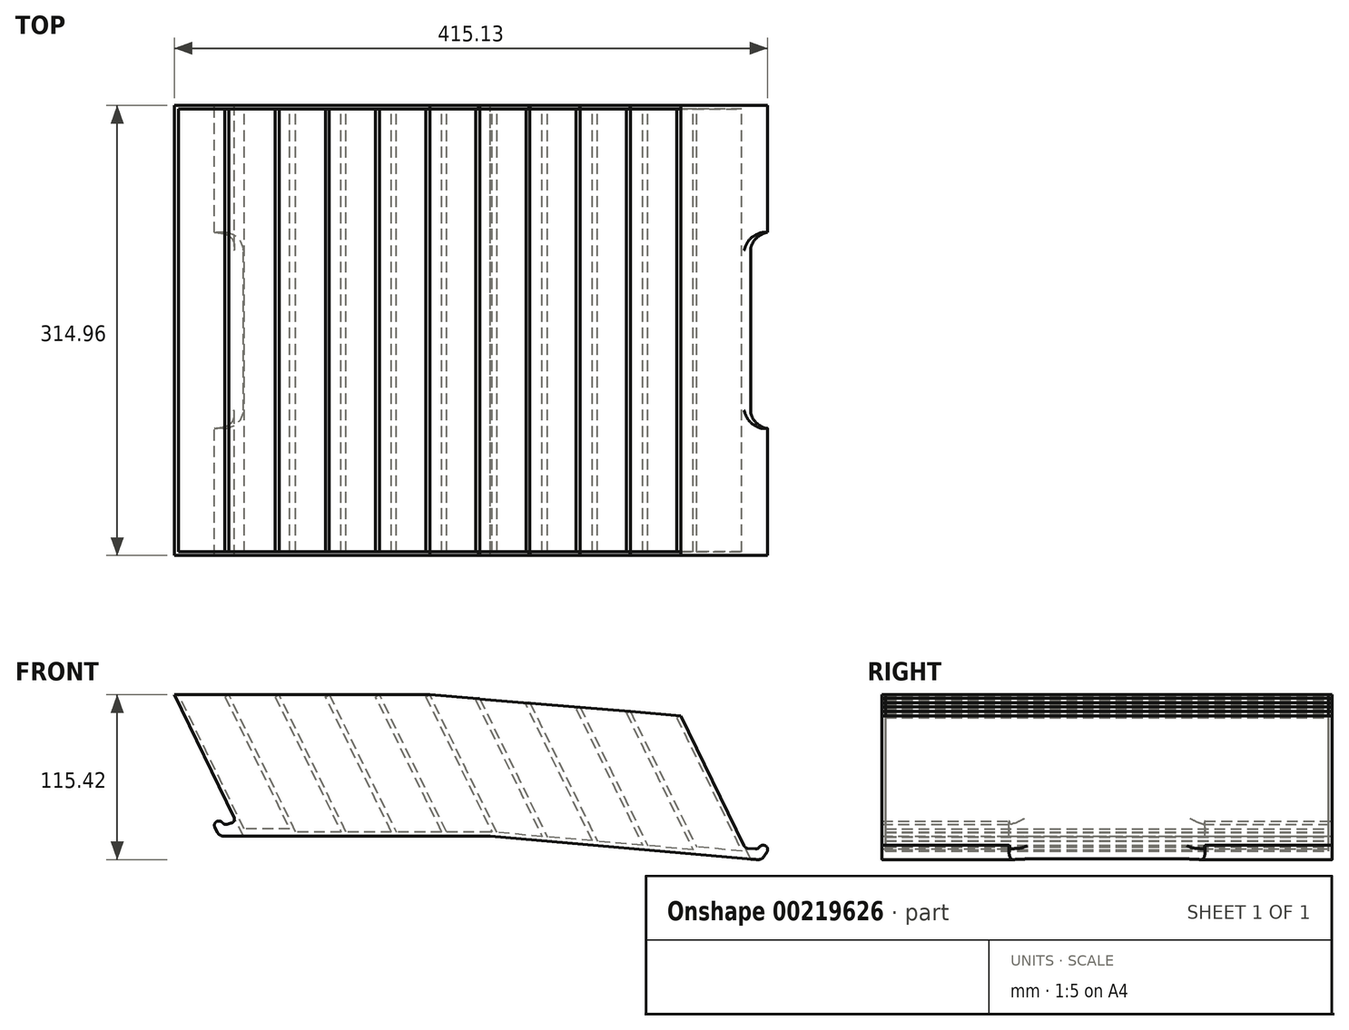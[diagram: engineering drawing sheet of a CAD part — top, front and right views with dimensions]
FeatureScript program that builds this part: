
annotation { "Feature Type Name" : "Feature", "Feature Type Description" : "" }
export const myFeature = defineFeature(function(context is Context, id is Id, definition is map)
    precondition{}
    {
        {
            var Q0;
            Q0=qCreatedBy(makeId("Front.planeOp"),FACE);
            var sketch = newSketch(context, id + "F0", { "sketchPlane" : qUnion([Q0])});
            skLineSegment(sketch, "E0", {"start": v(0, 0) * mm, "end": v(189.48, 0) * mm});
            skLineSegment(sketch, "E1", {"start": v(189.48, 0) * mm, "end": v(379.26, -16.6) * mm});
            skLineSegment(sketch, "E2", {"start": v(367.73, -8.25) * mm, "end": v(332.9, 63.16) * mm});
            skLineSegment(sketch, "E3", {"start": v(332.9, 63.16) * mm, "end": v(330.16, 61.83) * mm, "construction": true});
            skLineSegment(sketch, "E4", {"start": v(330.16, 61.83) * mm, "end": v(365.33, -10.29) * mm});
            skLineSegment(sketch, "E5", {"start": v(11.64, 10.16) * mm, "end": v(-21.71, 78.55) * mm});
            skLineSegment(sketch, "E6", {"start": v(-21.71, 78.55) * mm, "end": v(-18.66, 78.55) * mm});
            skLineSegment(sketch, "E7", {"start": v(-18.66, 78.55) * mm, "end": v(17.17, 5.08) * mm});
            skLineSegment(sketch, "E8", {"start": v(17.17, 5.08) * mm, "end": v(48.92, 5.08) * mm});
            skLineSegment(sketch, "E9", {"start": v(48.92, 5.08) * mm, "end": v(13.74, 77.21) * mm});
            skLineSegment(sketch, "E10", {"start": v(13.74, 77.21) * mm, "end": v(16.48, 78.55) * mm});
            skLineSegment(sketch, "E11", {"start": v(16.48, 78.55) * mm, "end": v(52.31, 5.08) * mm});
            skLineSegment(sketch, "E12", {"start": v(52.31, 5.08) * mm, "end": v(84.06, 5.08) * mm, "construction": true});
            skLineSegment(sketch, "E13", {"start": v(84.06, 5.08) * mm, "end": v(48.88, 77.21) * mm});
            skLineSegment(sketch, "E14", {"start": v(48.88, 77.21) * mm, "end": v(51.62, 78.55) * mm, "construction": true});
            skLineSegment(sketch, "E15", {"start": v(51.62, 78.55) * mm, "end": v(87.45, 5.08) * mm});
            skLineSegment(sketch, "E16", {"start": v(87.45, 5.08) * mm, "end": v(119.2, 5.08) * mm, "construction": true});
            skLineSegment(sketch, "E17", {"start": v(119.2, 5.08) * mm, "end": v(84.02, 77.21) * mm});
            skLineSegment(sketch, "E18", {"start": v(86.76, 78.55) * mm, "end": v(122.6, 5.08) * mm});
            skLineSegment(sketch, "E19", {"start": v(122.6, 5.08) * mm, "end": v(154.34, 5.08) * mm, "construction": true});
            skLineSegment(sketch, "E20", {"start": v(154.34, 5.08) * mm, "end": v(119.16, 77.21) * mm});
            skLineSegment(sketch, "E21", {"start": v(119.16, 77.21) * mm, "end": v(121.9, 78.55) * mm, "construction": true});
            skLineSegment(sketch, "E22", {"start": v(121.9, 78.55) * mm, "end": v(157.73, 5.08) * mm});
            skLineSegment(sketch, "E23", {"start": v(157.73, 5.08) * mm, "end": v(189.48, 5.08) * mm, "construction": true});
            skLineSegment(sketch, "E24", {"start": v(189.48, 0) * mm, "end": v(189.48, 5.08) * mm, "construction": true});
            skLineSegment(sketch, "E25", {"start": v(189.48, 5.08) * mm, "end": v(154.3, 77.21) * mm});
            skLineSegment(sketch, "E26", {"start": v(154.3, 77.21) * mm, "end": v(157.04, 78.55) * mm, "construction": true});
            skLineSegment(sketch, "E27", {"start": v(157.04, 78.55) * mm, "end": v(193.02, 4.8) * mm});
            skLineSegment(sketch, "E28", {"start": v(193.02, 4.8) * mm, "end": v(224.65, 2.02) * mm, "construction": true});
            skLineSegment(sketch, "E29", {"start": v(224.65, 2.02) * mm, "end": v(189.47, 74.14) * mm});
            skLineSegment(sketch, "E30", {"start": v(189.47, 74.14) * mm, "end": v(192.21, 75.47) * mm, "construction": true});
            skLineSegment(sketch, "E31", {"start": v(192.21, 75.47) * mm, "end": v(228.19, 1.71) * mm});
            skLineSegment(sketch, "E32", {"start": v(224.65, 2.02) * mm, "end": v(228.19, 1.71) * mm, "construction": true});
            skLineSegment(sketch, "E33", {"start": v(228.19, 1.71) * mm, "end": v(259.82, -1.05) * mm, "construction": true});
            skLineSegment(sketch, "E34", {"start": v(259.82, -1.05) * mm, "end": v(224.65, 71.06) * mm});
            skLineSegment(sketch, "E35", {"start": v(224.65, 71.06) * mm, "end": v(227.39, 72.4) * mm, "construction": true});
            skLineSegment(sketch, "E36", {"start": v(227.39, 72.4) * mm, "end": v(263.36, -1.36) * mm});
            skLineSegment(sketch, "E37", {"start": v(263.36, -1.36) * mm, "end": v(294.99, -4.13) * mm, "construction": true});
            skLineSegment(sketch, "E38", {"start": v(294.99, -4.13) * mm, "end": v(259.82, 67.98) * mm});
            skLineSegment(sketch, "E39", {"start": v(259.82, 67.98) * mm, "end": v(262.56, 69.32) * mm, "construction": true});
            skLineSegment(sketch, "E40", {"start": v(262.56, 69.32) * mm, "end": v(298.53, -4.44) * mm});
            skLineSegment(sketch, "E41", {"start": v(298.53, -4.44) * mm, "end": v(330.16, -7.2) * mm, "construction": true});
            skLineSegment(sketch, "E42", {"start": v(330.16, -7.2) * mm, "end": v(294.99, 64.9) * mm});
            skLineSegment(sketch, "E43", {"start": v(294.99, 64.9) * mm, "end": v(297.73, 66.24) * mm, "construction": true});
            skLineSegment(sketch, "E44", {"start": v(297.73, 66.24) * mm, "end": v(333.7, -7.52) * mm});
            skLineSegment(sketch, "E45", {"start": v(333.7, -7.52) * mm, "end": v(365.33, -10.29) * mm});
            skLineSegment(sketch, "E46", {"start": v(-18.66, 78.55) * mm, "end": v(157.04, 78.55) * mm, "construction": true});
            skLineSegment(sketch, "E47", {"start": v(157.04, 78.55) * mm, "end": v(332.9, 63.16) * mm, "construction": true});
            skLineSegment(sketch, "E48", {"start": v(84.02, 77.21) * mm, "end": v(86.76, 78.55) * mm, "construction": true});
            skLineSegment(sketch, "E49", {"start": v(367.73, -8.25) * mm, "end": v(376.94, -9.06) * mm});
            skLineSegment(sketch, "E50", {"start": v(379.26, -16.6) * mm, "end": v(383.77, -9.65) * mm});
            skArc(sketch, "E51", {"start": v(383.77, -9.65) * mm, "mid": v(380.63, -6.27) * mm, "end": v(376.94, -9.06) * mm});
            skLineSegment(sketch, "E52", {"start": v(376.94, -9.06) * mm, "end": v(383.77, -9.65) * mm, "construction": true});
            skLineSegment(sketch, "E53", {"start": v(0, 0) * mm, "end": v(-4.05, 7.62) * mm});
            skLineSegment(sketch, "E54", {"start": v(11.64, 10.16) * mm, "end": v(2.8, 7.62) * mm});
            skArc(sketch, "E55", {"start": v(2.8, 7.62) * mm, "mid": v(-0.62, 10.67) * mm, "end": v(-4.05, 7.62) * mm});
            skLineSegment(sketch, "E56", {"start": v(-4.05, 7.62) * mm, "end": v(2.8, 7.62) * mm, "construction": true});
            skLineSegment(sketch, "E57", {"start": v(-21.71, 78.55) * mm, "end": v(-31.72, 99.06) * mm});
            skLineSegment(sketch, "E58", {"start": v(-31.72, 99.06) * mm, "end": v(-28.67, 99.06) * mm});
            skLineSegment(sketch, "E59", {"start": v(-28.67, 99.06) * mm, "end": v(-18.66, 78.55) * mm});
            skLineSegment(sketch, "E60", {"start": v(13.74, 77.21) * mm, "end": v(3.73, 97.72) * mm});
            skLineSegment(sketch, "E61", {"start": v(3.73, 97.72) * mm, "end": v(6.47, 99.06) * mm});
            skLineSegment(sketch, "E62", {"start": v(6.47, 99.06) * mm, "end": v(16.48, 78.55) * mm});
            skLineSegment(sketch, "E63", {"start": v(48.88, 77.21) * mm, "end": v(38.87, 97.72) * mm});
            skLineSegment(sketch, "E64", {"start": v(38.87, 97.72) * mm, "end": v(41.61, 99.06) * mm});
            skLineSegment(sketch, "E65", {"start": v(41.61, 99.06) * mm, "end": v(51.62, 78.55) * mm});
            skLineSegment(sketch, "E66", {"start": v(109.16, 97.72) * mm, "end": v(111.9, 99.06) * mm});
            skLineSegment(sketch, "E67", {"start": v(259.82, 67.98) * mm, "end": v(249.49, 89.16) * mm});
            skLineSegment(sketch, "E68", {"start": v(249.49, 89.16) * mm, "end": v(252.23, 90.5) * mm});
            skLineSegment(sketch, "E69", {"start": v(252.23, 90.5) * mm, "end": v(262.56, 69.32) * mm});
            skLineSegment(sketch, "E70", {"start": v(330.16, 61.83) * mm, "end": v(319.83, 83) * mm});
            skLineSegment(sketch, "E71", {"start": v(319.83, 83) * mm, "end": v(322.57, 84.34) * mm});
            skLineSegment(sketch, "E72", {"start": v(322.57, 84.34) * mm, "end": v(332.9, 63.16) * mm});
            skLineSegment(sketch, "E73", {"start": v(154.3, 77.21) * mm, "end": v(144.3, 97.72) * mm});
            skLineSegment(sketch, "E74", {"start": v(294.99, 64.9) * mm, "end": v(284.66, 86.08) * mm});
            skLineSegment(sketch, "E75", {"start": v(189.47, 74.14) * mm, "end": v(179.15, 95.31) * mm});
            skLineSegment(sketch, "E76", {"start": v(-28.67, 99.06) * mm, "end": v(154.3, 99.06) * mm, "construction": true});
            skLineSegment(sketch, "E77", {"start": v(322.57, 84.34) * mm, "end": v(154.3, 99.06) * mm, "construction": true});
            skLineSegment(sketch, "E78", {"start": v(86.76, 78.55) * mm, "end": v(76.76, 99.06) * mm});
            skLineSegment(sketch, "E79", {"start": v(76.76, 99.06) * mm, "end": v(74.02, 97.72) * mm});
            skLineSegment(sketch, "E80", {"start": v(74.02, 97.72) * mm, "end": v(84.02, 77.21) * mm});
            skLineSegment(sketch, "E81", {"start": v(109.16, 97.72) * mm, "end": v(119.16, 77.21) * mm});
            skLineSegment(sketch, "E82", {"start": v(111.9, 99.06) * mm, "end": v(121.9, 78.55) * mm});
            skLineSegment(sketch, "E83", {"start": v(157.04, 78.55) * mm, "end": v(147.04, 99.06) * mm});
            skLineSegment(sketch, "E84", {"start": v(147.04, 99.06) * mm, "end": v(144.3, 97.72) * mm});
            skLineSegment(sketch, "E85", {"start": v(192.21, 75.47) * mm, "end": v(181.89, 96.65) * mm});
            skLineSegment(sketch, "E86", {"start": v(181.89, 96.65) * mm, "end": v(179.15, 95.31) * mm});
            skLineSegment(sketch, "E87", {"start": v(227.39, 72.4) * mm, "end": v(217.06, 93.57) * mm});
            skLineSegment(sketch, "E88", {"start": v(217.06, 93.57) * mm, "end": v(214.32, 92.23) * mm});
            skLineSegment(sketch, "E89", {"start": v(214.32, 92.23) * mm, "end": v(224.65, 71.06) * mm});
            skLineSegment(sketch, "E90", {"start": v(297.73, 66.24) * mm, "end": v(287.4, 87.42) * mm});
            skLineSegment(sketch, "E91", {"start": v(287.4, 87.42) * mm, "end": v(284.66, 86.08) * mm});
            skLineSegment(sketch, "E92", {"start": v(52.31, 5.08) * mm, "end": v(53.3, 3.05) * mm});
            skLineSegment(sketch, "E93", {"start": v(53.3, 3.05) * mm, "end": v(189.48, 3.05) * mm});
            skLineSegment(sketch, "E94", {"start": v(189.48, 3.05) * mm, "end": v(331.2, -9.35) * mm});
            skLineSegment(sketch, "E95", {"start": v(331.2, -9.35) * mm, "end": v(330.16, -7.2) * mm});
            skLineSegment(sketch, "E96", {"start": v(84.06, 5.08) * mm, "end": v(85.05, 3.05) * mm});
            skLineSegment(sketch, "E97", {"start": v(87.45, 5.08) * mm, "end": v(88.44, 3.05) * mm});
            skLineSegment(sketch, "E98", {"start": v(119.2, 5.08) * mm, "end": v(120.2, 3.05) * mm});
            skLineSegment(sketch, "E99", {"start": v(122.6, 5.08) * mm, "end": v(123.58, 3.05) * mm});
            skLineSegment(sketch, "E100", {"start": v(154.34, 5.08) * mm, "end": v(155.33, 3.05) * mm});
            skLineSegment(sketch, "E101", {"start": v(157.73, 5.08) * mm, "end": v(158.73, 3.05) * mm});
            skLineSegment(sketch, "E102", {"start": v(189.48, 5.08) * mm, "end": v(190.52, 2.96) * mm});
            skLineSegment(sketch, "E103", {"start": v(193.02, 4.8) * mm, "end": v(194.06, 2.65) * mm});
            skLineSegment(sketch, "E104", {"start": v(224.65, 2.02) * mm, "end": v(225.7, -0.12) * mm});
            skLineSegment(sketch, "E105", {"start": v(228.19, 1.71) * mm, "end": v(229.23, -0.43) * mm});
            skLineSegment(sketch, "E106", {"start": v(259.82, -1.05) * mm, "end": v(260.86, -3.2) * mm});
            skLineSegment(sketch, "E107", {"start": v(263.36, -1.36) * mm, "end": v(264.4, -3.5) * mm});
            skLineSegment(sketch, "E108", {"start": v(294.99, -4.13) * mm, "end": v(296.03, -6.27) * mm});
            skLineSegment(sketch, "E109", {"start": v(298.53, -4.44) * mm, "end": v(299.58, -6.58) * mm});
            skSolve(sketch);
        }
        {
            var Q0;
            Q0=qSketchRegion(id+"F0",true);
            extrude(context, id + "F1", {"entities" : qUnion([Q0]), "endBound" : BoundingType.SYMMETRIC, "depth" : 314.96 * mm});
        }
        {
            var Q0;
            Q0=makeQuery(id+"F1.opExtrude","SWEPT_EDGE",EDGE,{"disambiguationData":[OSD([sQuery(id+"F0.wireOp",EDGE,"E5"),sQuery(id+"F0.wireOp",EDGE,"E54")])]});
            var Q1;
            Q1=makeQuery(id+"F1.opExtrude","SWEPT_EDGE",EDGE,{"disambiguationData":[OSD([sQuery(id+"F0.wireOp",EDGE,"E54"),sQuery(id+"F0.wireOp",EDGE,"E55")])]});
            var Q2;
            Q2=makeQuery(id+"F1.opExtrude","SWEPT_EDGE",EDGE,{"disambiguationData":[OSD([sQuery(id+"F0.wireOp",EDGE,"E2"),sQuery(id+"F0.wireOp",EDGE,"E49")])]});
            var Q3;
            Q3=makeQuery(id+"F1.opExtrude","SWEPT_EDGE",EDGE,{"disambiguationData":[OSD([sQuery(id+"F0.wireOp",EDGE,"E49"),sQuery(id+"F0.wireOp",EDGE,"E51")])]});
            var Q4;
            Q4=makeQuery(id+"F1.opExtrude","SWEPT_EDGE",EDGE,{"disambiguationData":[OSD([sQuery(id+"F0.wireOp",EDGE,"E50"),sQuery(id+"F0.wireOp",EDGE,"E51")])]});
            var Q5;
            Q5=makeQuery(id+"F1.opExtrude","SWEPT_EDGE",EDGE,{"disambiguationData":[OSD([sQuery(id+"F0.wireOp",EDGE,"E53"),sQuery(id+"F0.wireOp",EDGE,"E55")])]});
            fillet(context, id + "F2", {"entities" : qUnion([Q0, Q1, Q2, Q3, Q4, Q5]), "radius" : 3.05 * mm, "tangentPropagation" : true, "allowEdgeOverflow" : false});
        }
        {
            var Q0;
            Q0=makeQuery(id+"F1.opExtrude","SWEPT_EDGE",EDGE,{"disambiguationData":[OSD([sQuery(id+"F0.wireOp",EDGE,"E0"),sQuery(id+"F0.wireOp",EDGE,"E53")])]});
            var Q1;
            Q1=makeQuery(id+"F1.opExtrude","SWEPT_EDGE",EDGE,{"disambiguationData":[OSD([sQuery(id+"F0.wireOp",EDGE,"E1"),sQuery(id+"F0.wireOp",EDGE,"E50")])]});
            fillet(context, id + "F3", {"entities" : qUnion([Q0, Q1]), "radius" : 5.08 * mm, "tangentPropagation" : true, "allowEdgeOverflow" : false});
        }
        {
            var Q0;
            Q0=makeQuery(id+"F1.opExtrude","CAP_FACE",FACE,{"disambiguationData":[OSD([sQuery(id+"F0.wireOp",EDGE,"E0"),sQuery(id+"F0.wireOp",EDGE,"E1"),sQuery(id+"F0.wireOp",EDGE,"E2"),sQuery(id+"F0.wireOp",EDGE,"E3"),sQuery(id+"F0.wireOp",EDGE,"E4"),sQuery(id+"F0.wireOp",EDGE,"E5"),sQuery(id+"F0.wireOp",EDGE,"E6"),sQuery(id+"F0.wireOp",EDGE,"E7"),sQuery(id+"F0.wireOp",EDGE,"E8"),sQuery(id+"F0.wireOp",EDGE,"E9"),sQuery(id+"F0.wireOp",EDGE,"E10"),sQuery(id+"F0.wireOp",EDGE,"E11"),sQuery(id+"F0.wireOp",EDGE,"E12"),sQuery(id+"F0.wireOp",EDGE,"E13"),sQuery(id+"F0.wireOp",EDGE,"E14"),sQuery(id+"F0.wireOp",EDGE,"E15"),sQuery(id+"F0.wireOp",EDGE,"E16"),sQuery(id+"F0.wireOp",EDGE,"E17"),sQuery(id+"F0.wireOp",EDGE,"E18"),sQuery(id+"F0.wireOp",EDGE,"E19"),sQuery(id+"F0.wireOp",EDGE,"E20"),sQuery(id+"F0.wireOp",EDGE,"E21"),sQuery(id+"F0.wireOp",EDGE,"E22"),sQuery(id+"F0.wireOp",EDGE,"E23"),sQuery(id+"F0.wireOp",EDGE,"E25"),sQuery(id+"F0.wireOp",EDGE,"E26"),sQuery(id+"F0.wireOp",EDGE,"E27"),sQuery(id+"F0.wireOp",EDGE,"E28"),sQuery(id+"F0.wireOp",EDGE,"E29"),sQuery(id+"F0.wireOp",EDGE,"E30"),sQuery(id+"F0.wireOp",EDGE,"E31"),sQuery(id+"F0.wireOp",EDGE,"E33"),sQuery(id+"F0.wireOp",EDGE,"E34"),sQuery(id+"F0.wireOp",EDGE,"E35"),sQuery(id+"F0.wireOp",EDGE,"E36"),sQuery(id+"F0.wireOp",EDGE,"E37"),sQuery(id+"F0.wireOp",EDGE,"E38"),sQuery(id+"F0.wireOp",EDGE,"E39"),sQuery(id+"F0.wireOp",EDGE,"E40"),sQuery(id+"F0.wireOp",EDGE,"E41"),sQuery(id+"F0.wireOp",EDGE,"E42"),sQuery(id+"F0.wireOp",EDGE,"E43"),sQuery(id+"F0.wireOp",EDGE,"E44"),sQuery(id+"F0.wireOp",EDGE,"E45"),sQuery(id+"F0.wireOp",EDGE,"E48"),sQuery(id+"F0.wireOp",EDGE,"E49"),sQuery(id+"F0.wireOp",EDGE,"E50"),sQuery(id+"F0.wireOp",EDGE,"E51"),sQuery(id+"F0.wireOp",EDGE,"E53"),sQuery(id+"F0.wireOp",EDGE,"E54"),sQuery(id+"F0.wireOp",EDGE,"E55")])],"isStart":false});
            var sketch = newSketch(context, id + "F4", { "sketchPlane" : qUnion([Q0])});
            skLineSegment(sketch, "E110.0", {"start": v(10.05, 13.42) * mm, "end": v(-31.72, 99.06) * mm});
            skArc(sketch, "E110.1", {"start": v(10.05, 13.42) * mm, "mid": v(10.1, 10.85) * mm, "end": v(8.15, 9.16) * mm});
            skLineSegment(sketch, "E110.2", {"start": v(8.15, 9.16) * mm, "end": v(5.3, 8.34) * mm});
            skArc(sketch, "E110.3", {"start": v(5.3, 8.34) * mm, "mid": v(3.53, 8.36) * mm, "end": v(2.08, 9.37) * mm});
            skArc(sketch, "E110.4", {"start": v(2.08, 9.37) * mm, "mid": v(0.97, 10.28) * mm, "end": v(-0.42, 10.66) * mm});
            skArc(sketch, "E110.5", {"start": v(-0.42, 10.66) * mm, "mid": v(-3.17, 9.26) * mm, "end": v(-3.3, 6.19) * mm});
            skLineSegment(sketch, "E110.6", {"start": v(-1.43, 2.7) * mm, "end": v(-3.3, 6.19) * mm});
            skArc(sketch, "E110.7", {"start": v(-1.43, 2.7) * mm, "mid": v(0.44, 0.73) * mm, "end": v(3.05, 0) * mm});
            skLineSegment(sketch, "E110.8", {"start": v(3.05, 0) * mm, "end": v(189.48, 0) * mm});
            skLineSegment(sketch, "E110.9", {"start": v(189.48, 0) * mm, "end": v(376.22, -16.34) * mm});
            skLineSegment(sketch, "E110.10", {"start": v(366.98, -6.7) * mm, "end": v(322.57, 84.34) * mm});
            skArc(sketch, "E110.11", {"start": v(369.45, -8.4) * mm, "mid": v(367.99, -7.88) * mm, "end": v(366.98, -6.7) * mm});
            skLineSegment(sketch, "E110.12", {"start": v(369.45, -8.4) * mm, "end": v(374.84, -8.87) * mm});
            skArc(sketch, "E110.13", {"start": v(377.56, -7.65) * mm, "mid": v(376.36, -8.62) * mm, "end": v(374.84, -8.87) * mm});
            skArc(sketch, "E110.14", {"start": v(380.66, -6.27) * mm, "mid": v(378.93, -6.55) * mm, "end": v(377.56, -7.65) * mm});
            skArc(sketch, "E110.15", {"start": v(382.92, -10.97) * mm, "mid": v(383.1, -7.98) * mm, "end": v(380.66, -6.27) * mm});
            skLineSegment(sketch, "E110.16", {"start": v(380.92, -14.04) * mm, "end": v(382.92, -10.97) * mm});
            skArc(sketch, "E110.17", {"start": v(376.22, -16.34) * mm, "mid": v(378.89, -15.84) * mm, "end": v(380.92, -14.04) * mm});
            skLineSegment(sketch, "E111", {"start": v(322.57, 84.34) * mm, "end": v(147.04, 99.06) * mm});
            skLineSegment(sketch, "E112", {"start": v(147.04, 99.06) * mm, "end": v(-31.72, 99.06) * mm});
            skSolve(sketch);
        }
        {
            var Q0;
            Q0=qSketchRegion(id+"F4",true);
            extrude(context, id + "F5", {"entities" : qUnion([Q0]), "oppositeDirection" : true, "depth" : 2.54 * mm});
        }
        {
            var Q0;
            Q0=makeQuery(id+"F5.opExtrude","SWEPT_BODY",BODY,{"disambiguationData":[OSD([sQuery(id+"F4.wireOp",EDGE,"E110.0"),sQuery(id+"F4.wireOp",EDGE,"E110.1"),sQuery(id+"F4.wireOp",EDGE,"E110.2"),sQuery(id+"F4.wireOp",EDGE,"E110.3"),sQuery(id+"F4.wireOp",EDGE,"E110.4"),sQuery(id+"F4.wireOp",EDGE,"E110.5"),sQuery(id+"F4.wireOp",EDGE,"E110.6"),sQuery(id+"F4.wireOp",EDGE,"E110.7"),sQuery(id+"F4.wireOp",EDGE,"E110.8"),sQuery(id+"F4.wireOp",EDGE,"E110.9"),sQuery(id+"F4.wireOp",EDGE,"E110.10"),sQuery(id+"F4.wireOp",EDGE,"E110.11"),sQuery(id+"F4.wireOp",EDGE,"E110.12"),sQuery(id+"F4.wireOp",EDGE,"E110.13"),sQuery(id+"F4.wireOp",EDGE,"E110.14"),sQuery(id+"F4.wireOp",EDGE,"E110.15"),sQuery(id+"F4.wireOp",EDGE,"E110.16"),sQuery(id+"F4.wireOp",EDGE,"E110.17"),sQuery(id+"F4.wireOp",EDGE,"E111"),sQuery(id+"F4.wireOp",EDGE,"E112")])]});
            var Q1;
            Q1=qCreatedBy(makeId("Front.planeOp"),FACE);
            mirror(context, id + "F6", {"operationType" : NewBodyOperationType.ADD, "entities" : qUnion([Q0]), "mirrorPlane" : qUnion([Q1])});
        }
        {
            var Q0;
            Q0=makeQuery(id+"F1.opExtrude","SWEPT_FACE",FACE,{"disambiguationData":[OSD([sQuery(id+"F0.wireOp",EDGE,"E61")])]});
            var sketch = newSketch(context, id + "F7", { "sketchPlane" : qUnion([Q0])});
            skLineSegment(sketch, "E113.bottom", {"start": v(14.92, -68.58) * mm, "end": v(-14.92, -68.58) * mm});
            skLineSegment(sketch, "E113.top", {"start": v(14.92, 68.58) * mm, "end": v(-14.92, 68.58) * mm});
            skLineSegment(sketch, "E113.left", {"start": v(14.92, -68.58) * mm, "end": v(14.92, 68.58) * mm});
            skLineSegment(sketch, "E113.right", {"start": v(-14.92, -68.58) * mm, "end": v(-14.92, 68.58) * mm});
            skPoint(sketch, "E113.middle", {"position": v(0, 0) * mm});
            skSolve(sketch);
        }
        {
            var Q0;
            Q0=qSketchRegion(id+"F7",true);
            extrude(context, id + "F8", {"entities" : qUnion([Q0]), "operationType" : NewBodyOperationType.REMOVE, "oppositeDirection" : true, "depth" : 144.78 * mm});
        }
        {
            var Q0;
            Q0=makeQuery(id+"F1.opExtrude","SWEPT_FACE",FACE,{"disambiguationData":[OSD([sQuery(id+"F0.wireOp",EDGE,"E61")])]});
            var sketch = newSketch(context, id + "F9", { "sketchPlane" : qUnion([Q0])});
            skLineSegment(sketch, "E114.bottom", {"start": v(326.9, -68.58) * mm, "end": v(466.95, -68.58) * mm});
            skLineSegment(sketch, "E114.top", {"start": v(326.9, 68.58) * mm, "end": v(466.95, 68.58) * mm});
            skLineSegment(sketch, "E114.left", {"start": v(326.9, -68.58) * mm, "end": v(326.9, 68.58) * mm});
            skLineSegment(sketch, "E114.right", {"start": v(466.95, -68.58) * mm, "end": v(466.95, 68.58) * mm});
            skPoint(sketch, "E114.middle", {"position": v(396.93, 0) * mm});
            skSolve(sketch);
        }
        {
            var Q0;
            Q0=qSketchRegion(id+"F9",true);
            extrude(context, id + "F10", {"entities" : qUnion([Q0]), "operationType" : NewBodyOperationType.REMOVE, "oppositeDirection" : true, "depth" : 293.12 * mm});
        }
        {
            var Q0;
            Q0=makeQuery(id+"F10.boolean.opBoolean","COPY",EDGE,{"derivedFrom":makeQuery(id+"F10.opExtrude","SWEPT_EDGE",EDGE,{"disambiguationData":[OSD([sQuery(id+"F9.wireOp",EDGE,"E114.bottom"),sQuery(id+"F9.wireOp",EDGE,"E114.left")])]})});
            var Q1;
            Q1=makeQuery(id+"F10.boolean.opBoolean","COPY",EDGE,{"derivedFrom":makeQuery(id+"F10.opExtrude","SWEPT_EDGE",EDGE,{"disambiguationData":[OSD([sQuery(id+"F9.wireOp",EDGE,"E114.top"),sQuery(id+"F9.wireOp",EDGE,"E114.left")])]})});
            var Q2;
            Q2=makeQuery(id+"F8.boolean.opBoolean","COPY",EDGE,{"derivedFrom":makeQuery(id+"F8.opExtrude","SWEPT_EDGE",EDGE,{"disambiguationData":[OSD([sQuery(id+"F7.wireOp",EDGE,"E113.top"),sQuery(id+"F7.wireOp",EDGE,"E113.left")])]})});
            var Q3;
            Q3=makeQuery(id+"F8.boolean.opBoolean","COPY",EDGE,{"derivedFrom":makeQuery(id+"F8.opExtrude","SWEPT_EDGE",EDGE,{"disambiguationData":[OSD([sQuery(id+"F7.wireOp",EDGE,"E113.bottom"),sQuery(id+"F7.wireOp",EDGE,"E113.left")])]})});
            fillet(context, id + "F11", {"entities" : qUnion([Q0, Q1, Q2, Q3]), "radius" : 12.7 * mm, "tangentPropagation" : true, "allowEdgeOverflow" : false});
        }
    });
